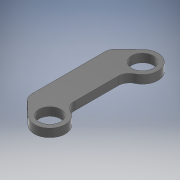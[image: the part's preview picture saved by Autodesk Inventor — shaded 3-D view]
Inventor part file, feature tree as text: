
AUTODESK INVENTOR PART (.ipt)
format: ipt  version: 2022 (Build 260153000, 153)  size: 145,408 bytes
history: native  units: mm
features: sketch x2, hole x2, fillet x2, extrude x1
ambient origin geometry x8: Origin, YZ Plane, XZ Plane, XY Plane, X Axis, Y Axis, Z Axis, Center Point
bodies: Body1 (feature_tree)
feature tree (7):
  sketch  "Sketch1"  dims[d20=16.0mm d21=0.0mm]
  extrude  "Extrusion2"  Depth=22.0mm
  hole  "Hole3"  [1 undecoded]
  fillet  "Fillet3"  [1 undecoded]
  sketch  "Sketch4"  dims[d22=42.0mm d23=18.0mm d24=4.0mm d25=2.0mm d26=90.0deg d27=20.0mm d28=0.0mm d29=22.0mm d30=22.0mm d31=6.647mm d32=18.0mm d33=4.0mm d34=2.0mm d35=90.0deg d36=20.0mm d37=20.594885mm]
  fillet  "Fillet4"  [1 undecoded]
  hole  "Hole4"  [1 undecoded]
note: 4 required parameter values undecoded (feature->parameter linkage not recoverable at this tier; creation-order binding heuristic only, values carry confidence <= 0.55)
